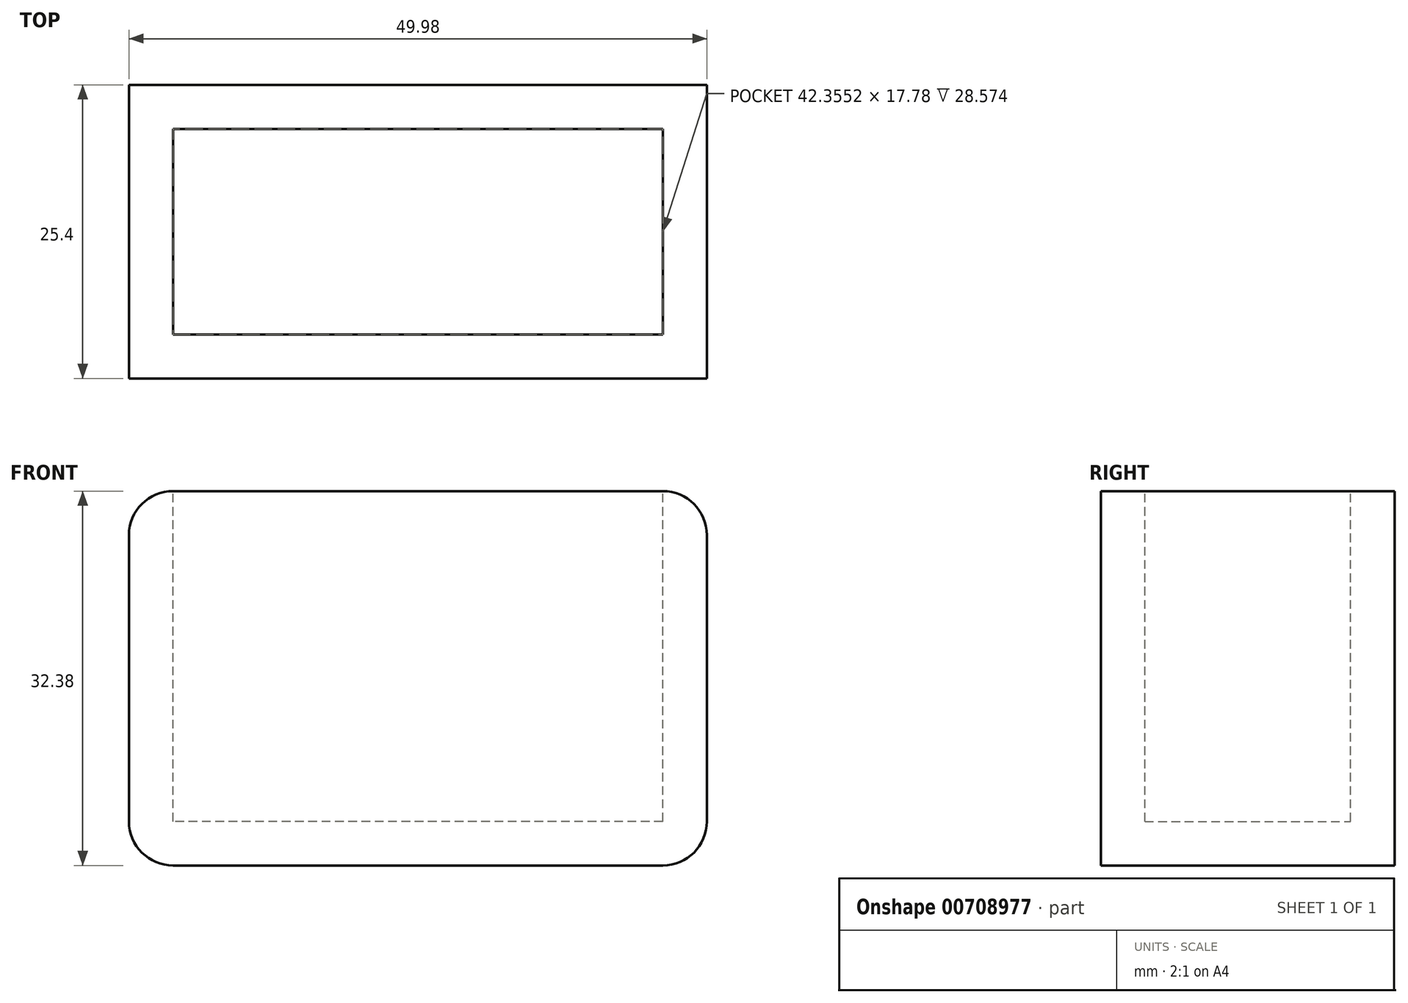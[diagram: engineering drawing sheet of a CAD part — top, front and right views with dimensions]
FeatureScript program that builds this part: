
annotation { "Feature Type Name" : "Feature", "Feature Type Description" : "" }
export const myFeature = defineFeature(function(context is Context, id is Id, definition is map)
    precondition{}
    {
        {
            var Q0;
            Q0=qCreatedBy(makeId("Front.planeOp"),FACE);
            var sketch = newSketch(context, id + "F0", { "sketchPlane" : qUnion([Q0])});
            skLineSegment(sketch, "E0.bottom", {"start": v(21.18, -16.2) * mm, "end": v(-21.18, -16.2) * mm});
            skLineSegment(sketch, "E0.top", {"start": v(21.18, 16.2) * mm, "end": v(-21.18, 16.2) * mm});
            skLineSegment(sketch, "E0.left", {"start": v(24.99, -12.38) * mm, "end": v(24.99, 12.38) * mm});
            skLineSegment(sketch, "E0.right", {"start": v(-24.99, -12.38) * mm, "end": v(-24.99, 12.38) * mm});
            skPoint(sketch, "E0.middle", {"position": v(0, 0) * mm});
            skPoint(sketch, "E1.visualSharp", {"position": v(-24.99, 16.2) * mm});
            skArc(sketch, "E1.filletArc", {"start": v(-21.18, 16.2) * mm, "mid": v(-23.87, 15.08) * mm, "end": v(-24.99, 12.38) * mm});
            skPoint(sketch, "E2.visualSharp", {"position": v(24.99, 16.2) * mm});
            skArc(sketch, "E2.filletArc", {"start": v(24.99, 12.38) * mm, "mid": v(23.87, 15.08) * mm, "end": v(21.18, 16.2) * mm});
            skPoint(sketch, "E3.visualSharp", {"position": v(-24.99, -16.2) * mm});
            skArc(sketch, "E3.filletArc", {"start": v(-24.99, -12.38) * mm, "mid": v(-23.87, -15.08) * mm, "end": v(-21.18, -16.2) * mm});
            skPoint(sketch, "E4.visualSharp", {"position": v(24.99, -16.2) * mm});
            skArc(sketch, "E4.filletArc", {"start": v(21.18, -16.2) * mm, "mid": v(23.87, -15.08) * mm, "end": v(24.99, -12.38) * mm});
            skSolve(sketch);
        }
        {
            var Q0;
            Q0=qSketchRegion(id+"F0",true);
            extrude(context, id + "F1", {"entities" : qUnion([Q0]), "depth" : 25.4 * mm, "offsetDistance" : 25.4 * mm});
        }
        {
            var Q0;
            Q0=makeQuery(id+"F1.opExtrude","SWEPT_FACE",FACE,{"disambiguationData":[OSD([sQuery(id+"F0.wireOp",EDGE,"E0.top")])]});
            shell(context, id + "F2", {"entities" : qUnion([Q0]), "thickness" : 3.8 * mm});
        }
    });
